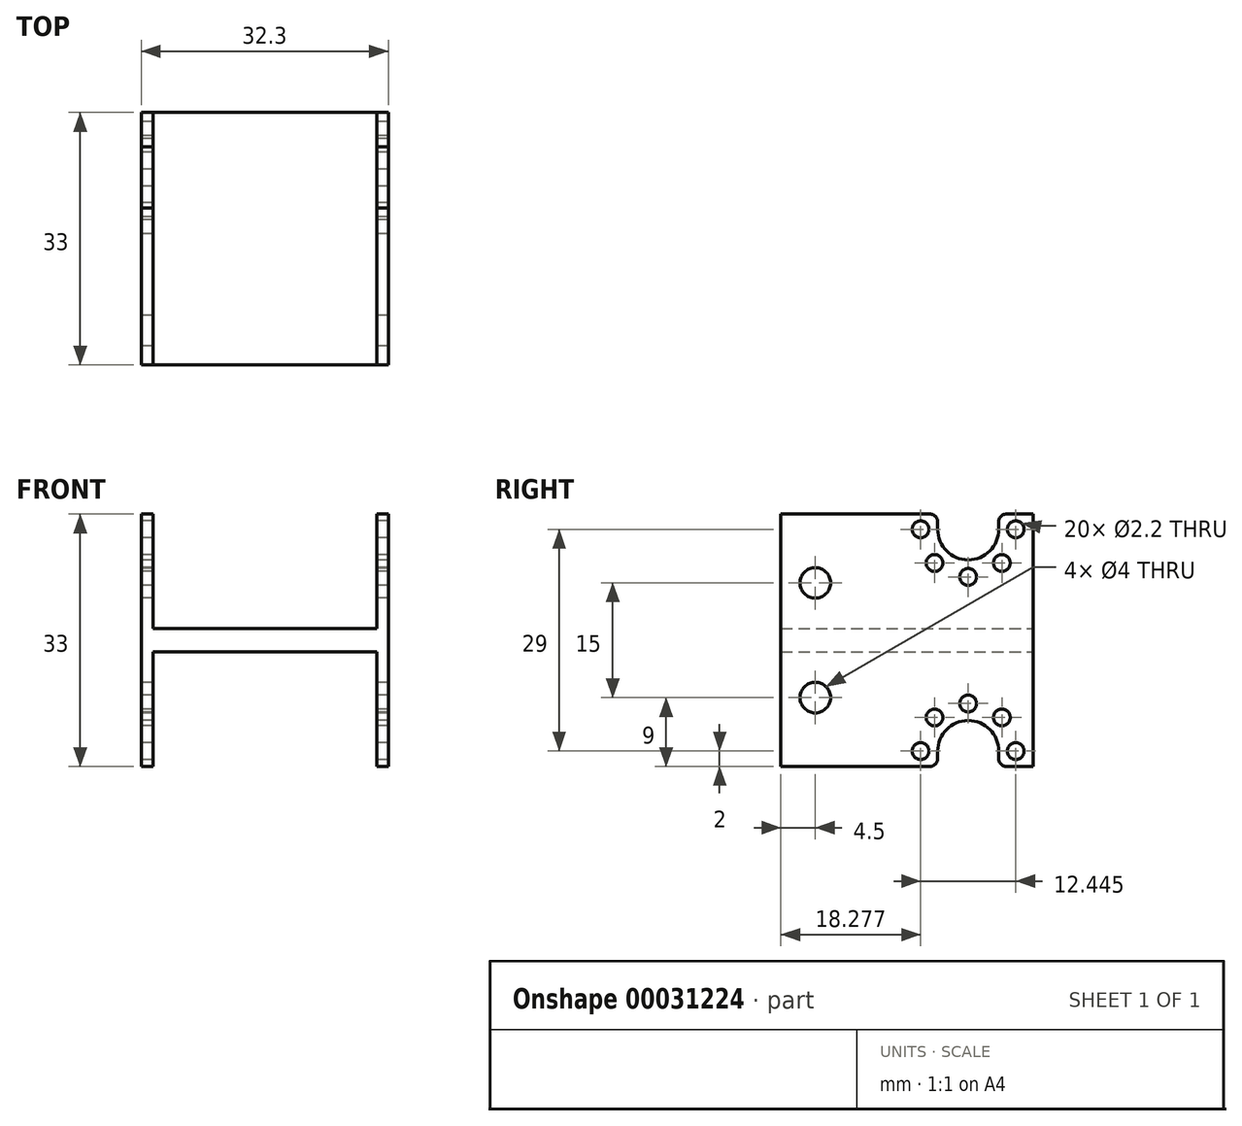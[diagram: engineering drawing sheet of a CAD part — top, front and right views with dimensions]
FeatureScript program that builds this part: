
annotation { "Feature Type Name" : "Feature", "Feature Type Description" : "" }
export const myFeature = defineFeature(function(context is Context, id is Id, definition is map)
    precondition{}
    {
        {
            var Q0;
            Q0=qCreatedBy(makeId("Front.planeOp"),FACE);
            var sketch = newSketch(context, id + "F0", { "sketchPlane" : qUnion([Q0])});
            skLineSegment(sketch, "E0.bottom", {"start": v(0, 0) * mm, "end": v(1.5, 0) * mm});
            skLineSegment(sketch, "E0.top", {"start": v(0, 26.5) * mm, "end": v(32.3, 26.5) * mm});
            skLineSegment(sketch, "E0.left", {"start": v(0, 0) * mm, "end": v(0, 26.5) * mm});
            skLineSegment(sketch, "E0.right", {"start": v(32.3, 0) * mm, "end": v(32.3, 26.5) * mm});
            skLineSegment(sketch, "E1.top", {"start": v(1.5, 25) * mm, "end": v(30.8, 25) * mm});
            skLineSegment(sketch, "E1.left", {"start": v(1.5, 0) * mm, "end": v(1.5, 25) * mm});
            skLineSegment(sketch, "E1.right", {"start": v(30.8, 0) * mm, "end": v(30.8, 25) * mm});
            skLineSegment(sketch, "E2.trimOffspring", {"start": v(30.8, 0) * mm, "end": v(32.3, 0) * mm});
            skSolve(sketch);
        }
        {
            var Q0;
            Q0=qSketchRegion(id+"F0",true);
            extrude(context, id + "F1", {"entities" : qUnion([Q0]), "depth" : 33 * mm});
        }
        {
            var Q0;
            Q0=makeQuery(id+"F1.opExtrude","SWEPT_FACE",FACE,{"disambiguationData":[OSD([sQuery(id+"F0.wireOp",EDGE,"E0.left")])]});
            var sketch = newSketch(context, id + "F2", { "sketchPlane" : qUnion([Q0])});
            skLineSegment(sketch, "E3.bottom", {"start": v(0, 0) * mm, "end": v(33, 0) * mm});
            skLineSegment(sketch, "E3.top", {"start": v(0, 10) * mm, "end": v(4.5, 10) * mm});
            skLineSegment(sketch, "E3.left", {"start": v(0, 0) * mm, "end": v(0, 10) * mm});
            skLineSegment(sketch, "E3.right", {"start": v(33, 0) * mm, "end": v(33, 10) * mm});
            skArc(sketch, "E4", {"start": v(12.5, 12) * mm, "mid": v(8.5, 16) * mm, "end": v(4.5, 12) * mm});
            skCircle(sketch, "E5", {"center": v(14.72, 12) * mm, "radius": 1.1 * mm});
            skCircle(sketch, "E6.1.0", {"center": v(12.9, 16.4) * mm, "radius": 1.1 * mm});
            skCircle(sketch, "E6.2.0", {"center": v(8.5, 18.22) * mm, "radius": 1.1 * mm});
            skCircle(sketch, "E6.3.0", {"center": v(4.1, 16.4) * mm, "radius": 1.1 * mm});
            skCircle(sketch, "E6.4.0", {"center": v(2.28, 12) * mm, "radius": 1.1 * mm});
            skLineSegment(sketch, "E7", {"start": v(4.5, 12) * mm, "end": v(4.5, 10) * mm});
            skLineSegment(sketch, "E8", {"start": v(12.5, 12) * mm, "end": v(12.5, 10) * mm});
            skLineSegment(sketch, "E9.trimOffspring", {"start": v(12.5, 10) * mm, "end": v(33, 10) * mm});
            skCircle(sketch, "E10", {"center": v(28.5, 19) * mm, "radius": 2 * mm});
            skSolve(sketch);
        }
        {
            var Q0;
            Q0=qSketchRegion(id+"F2",true);
            extrude(context, id + "F3", {"entities" : qUnion([Q0]), "operationType" : NewBodyOperationType.REMOVE, "endBound" : BoundingType.THROUGH_ALL, "oppositeDirection" : true, "depth" : 25 * mm});
        }
        {
            var Q0;
            Q0=makeQuery(id+"F3.boolean.opBoolean","COPY",EDGE,{"disambiguationData":[OD(1.0)],"derivedFrom":makeQuery(id+"F3.opExtrude","SWEPT_EDGE",EDGE,{"disambiguationData":[OSD([sQuery(id+"F0.wireOp",EDGE,"E0.left"),sQuery(id+"F2.wireOp",EDGE,"E3.top"),sQuery(id+"F2.wireOp",EDGE,"E3.left")])]})});
            var Q1;
            Q1=makeQuery(id+"F3.boolean.opBoolean","COPY",EDGE,{"disambiguationData":[OD(1.0)],"derivedFrom":makeQuery(id+"F3.opExtrude","SWEPT_EDGE",EDGE,{"disambiguationData":[OSD([sQuery(id+"F2.wireOp",EDGE,"E8"),sQuery(id+"F2.wireOp",EDGE,"E9.trimOffspring")])]})});
            var Q2;
            Q2=makeQuery(id+"F3.boolean.opBoolean","COPY",EDGE,{"disambiguationData":[OD(1.0)],"derivedFrom":makeQuery(id+"F3.opExtrude","SWEPT_EDGE",EDGE,{"disambiguationData":[OSD([sQuery(id+"F2.wireOp",EDGE,"E3.top"),sQuery(id+"F2.wireOp",EDGE,"E7")])]})});
            var Q3;
            Q3=makeQuery(id+"F3.boolean.opBoolean","COPY",EDGE,{"disambiguationData":[OD(0.0)],"derivedFrom":makeQuery(id+"F3.opExtrude","SWEPT_EDGE",EDGE,{"disambiguationData":[OSD([sQuery(id+"F0.wireOp",EDGE,"E0.left"),sQuery(id+"F2.wireOp",EDGE,"E3.top"),sQuery(id+"F2.wireOp",EDGE,"E3.left")])]})});
            var Q4;
            Q4=makeQuery(id+"F3.boolean.opBoolean","COPY",EDGE,{"disambiguationData":[OD(0.0)],"derivedFrom":makeQuery(id+"F3.opExtrude","SWEPT_EDGE",EDGE,{"disambiguationData":[OSD([sQuery(id+"F2.wireOp",EDGE,"E8"),sQuery(id+"F2.wireOp",EDGE,"E9.trimOffspring")])]})});
            var Q5;
            Q5=makeQuery(id+"F3.boolean.opBoolean","COPY",EDGE,{"disambiguationData":[OD(1.0)],"derivedFrom":makeQuery(id+"F3.opExtrude","SWEPT_EDGE",EDGE,{"disambiguationData":[OSD([sQuery(id+"F0.wireOp",EDGE,"E0.left"),sQuery(id+"F2.wireOp",EDGE,"E3.right"),sQuery(id+"F2.wireOp",EDGE,"E9.trimOffspring")])]})});
            var Q6;
            Q6=makeQuery(id+"F3.boolean.opBoolean","COPY",EDGE,{"disambiguationData":[OD(0.0)],"derivedFrom":makeQuery(id+"F3.opExtrude","SWEPT_EDGE",EDGE,{"disambiguationData":[OSD([sQuery(id+"F0.wireOp",EDGE,"E0.left"),sQuery(id+"F2.wireOp",EDGE,"E3.right"),sQuery(id+"F2.wireOp",EDGE,"E9.trimOffspring")])]})});
            var Q7;
            Q7=makeQuery(id+"F3.boolean.opBoolean","COPY",EDGE,{"disambiguationData":[OD(0.0)],"derivedFrom":makeQuery(id+"F3.opExtrude","SWEPT_EDGE",EDGE,{"disambiguationData":[OSD([sQuery(id+"F2.wireOp",EDGE,"E3.top"),sQuery(id+"F2.wireOp",EDGE,"E7")])]})});
            fillet(context, id + "F4", {"entities" : qUnion([Q0, Q1, Q2, Q3, Q4, Q5, Q6, Q7]), "radius" : 1 * mm, "tangentPropagation" : true, "allowEdgeOverflow" : false});
        }
        {
            var Q0;
            Q0=qCreatedBy(makeId("Top.planeOp"),FACE);
            cPlane(context, id + "F5", {"entities" : qUnion([Q0]), "cplaneType" : CPlaneType.OFFSET, "offset" : 26.5 * mm, "width" : 150 * mm, "height" : 150 * mm});
        }
        {
            var Q0;
            Q0=makeQuery(id+"F1.opExtrude","SWEPT_BODY",BODY,{"disambiguationData":[OSD([sQuery(id+"F0.wireOp",EDGE,"E0.bottom"),sQuery(id+"F0.wireOp",EDGE,"E0.top"),sQuery(id+"F0.wireOp",EDGE,"E0.left"),sQuery(id+"F0.wireOp",EDGE,"E0.right"),sQuery(id+"F0.wireOp",EDGE,"E1.top"),sQuery(id+"F0.wireOp",EDGE,"E1.left"),sQuery(id+"F0.wireOp",EDGE,"E1.right"),sQuery(id+"F0.wireOp",EDGE,"E2.trimOffspring")])]});
            var Q1;
            Q1=qCreatedBy(id+"F5.planeOp",FACE);
            mirror(context, id + "F6", {"operationType" : NewBodyOperationType.ADD, "entities" : qUnion([Q0]), "mirrorPlane" : qUnion([Q1])});
        }
    });
